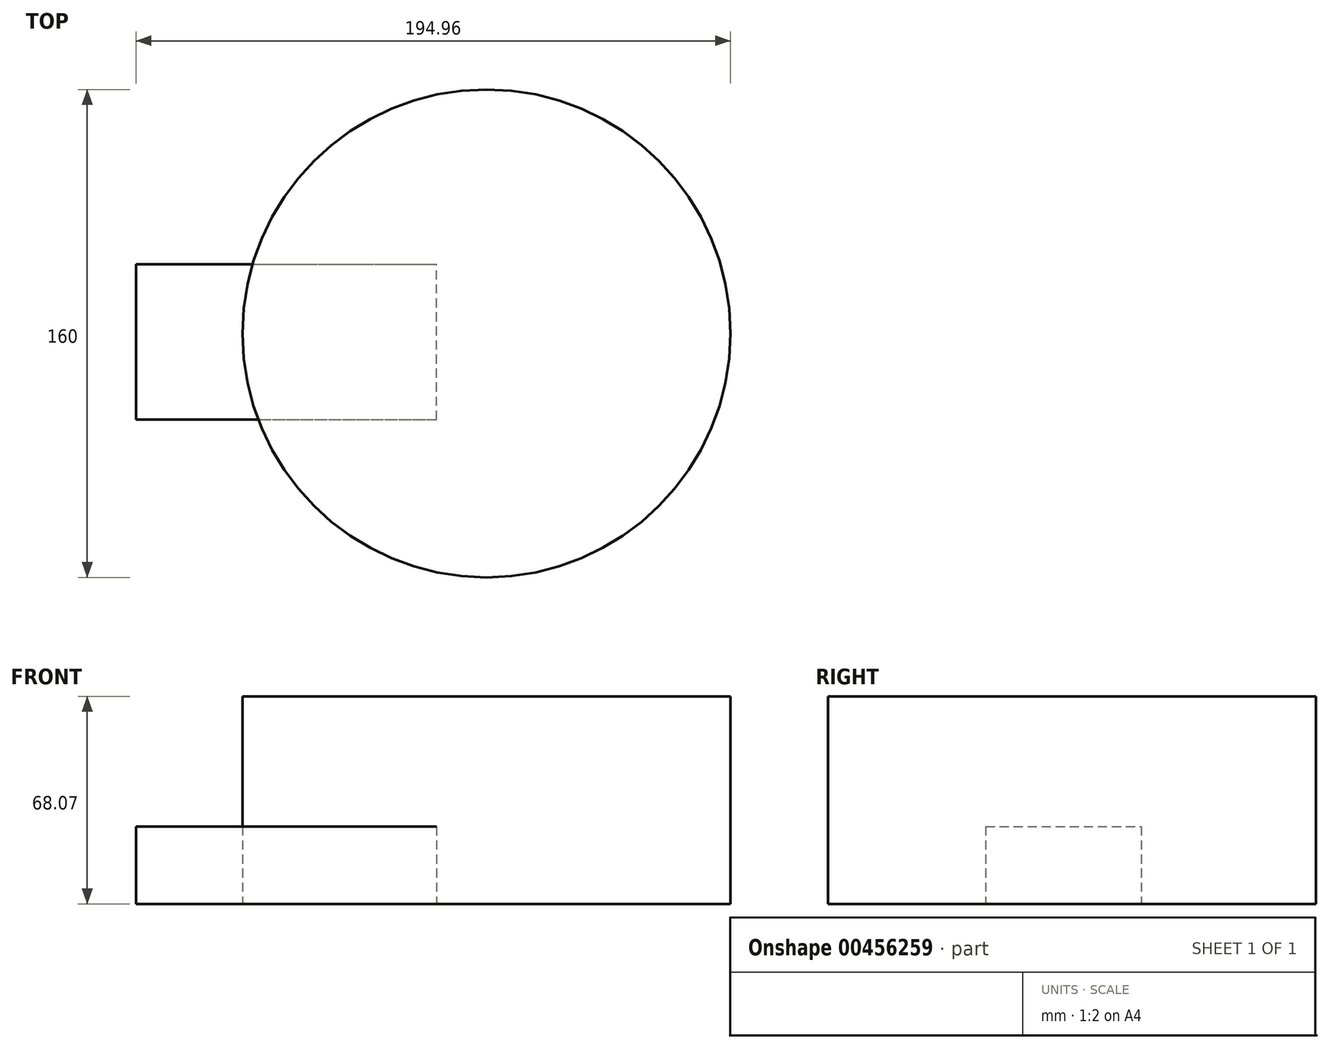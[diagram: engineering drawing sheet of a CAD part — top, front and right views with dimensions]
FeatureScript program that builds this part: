
annotation { "Feature Type Name" : "Feature", "Feature Type Description" : "" }
export const myFeature = defineFeature(function(context is Context, id is Id, definition is map)
    precondition{}
    {
        {
            var Q0;
            Q0=qCreatedBy(makeId("Top.planeOp"),FACE);
            var sketch = newSketch(context, id + "F0", { "sketchPlane" : qUnion([Q0])});
            skLineSegment(sketch, "E0.bottom", {"start": v(-138.45, -14.62) * mm, "end": v(-39.88, -14.62) * mm});
            skLineSegment(sketch, "E0.top", {"start": v(-138.45, 36.38) * mm, "end": v(-39.88, 36.38) * mm});
            skLineSegment(sketch, "E0.left", {"start": v(-138.45, -14.62) * mm, "end": v(-138.45, 36.38) * mm});
            skLineSegment(sketch, "E0.right", {"start": v(-39.88, -14.62) * mm, "end": v(-39.88, 36.38) * mm});
            skSolve(sketch);
        }
        {
            var Q0;
            Q0 = qSketchRegion(id + "F0", true);
            extrude(context, id + "F1", {"entities" : qUnion([Q0]), "depth" : 25.4 * mm, "offsetDistance" : 25.4 * mm});
        }
        {
            var Q0;
            Q0=qCreatedBy(makeId("Top.planeOp"),FACE);
            var sketch = newSketch(context, id + "F2", { "sketchPlane" : qUnion([Q0])});
            skCircle(sketch, "E1", {"center": v(-23.49, 13.68) * mm, "radius": 80 * mm});
            skSolve(sketch);
        }
        {
            var Q0;
            Q0 = qSketchRegion(id + "F2", true);
            extrude(context, id + "F3", {"entities" : qUnion([Q0]), "depth" : 68.07 * mm, "offsetDistance" : 25.4 * mm});
        }
    });
